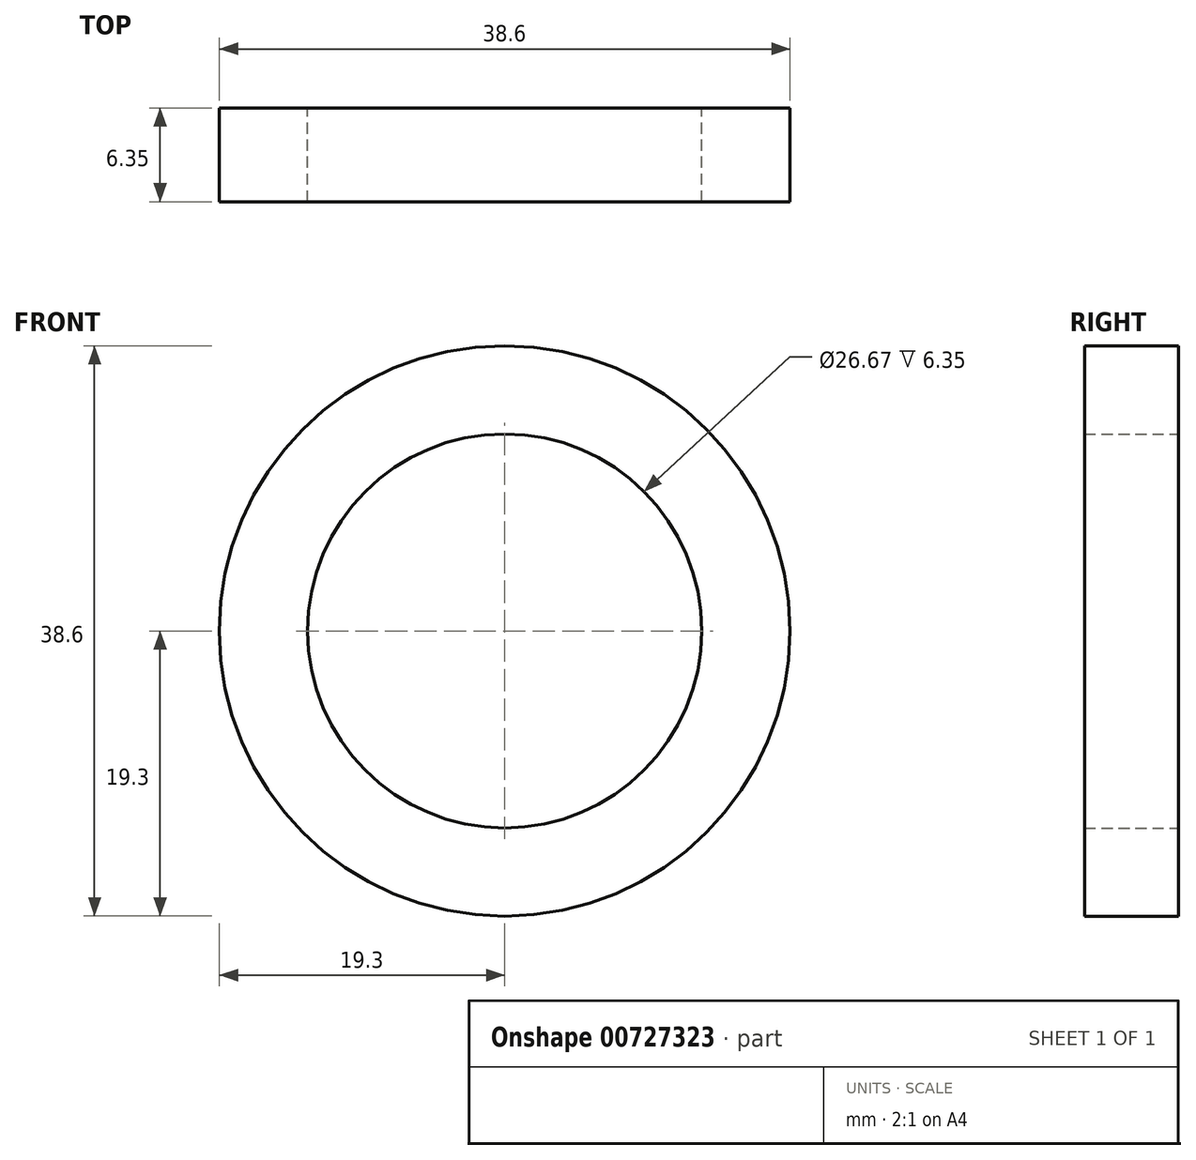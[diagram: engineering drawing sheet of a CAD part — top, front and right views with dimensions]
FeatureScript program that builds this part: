
annotation { "Feature Type Name" : "Feature", "Feature Type Description" : "" }
export const myFeature = defineFeature(function(context is Context, id is Id, definition is map)
    precondition{}
    {
        {
            var Q0;
            Q0=qCreatedBy(makeId("Front.planeOp"),FACE);
            var sketch = newSketch(context, id + "F0", { "sketchPlane" : qUnion([Q0])});
            skCircle(sketch, "E0", {"center": v(0, 0) * mm, "radius": 19.3 * mm});
            skCircle(sketch, "E1", {"center": v(0, 0) * mm, "radius": 13.33 * mm});
            skSolve(sketch);
        }
        {
            var Q0;
            Q0=makeQuery(id+"F0.imprint","IMPRINT",FACE,{"disambiguationData":[TD([[makeQuery(id+"F0.imprint","IMPRINT",EDGE,{"derivedFrom":sQuery(id+"F0.wireOp",EDGE,"E0")}),1.0]])]});
            extrude(context, id + "F1", {"entities" : qUnion([Q0]), "depth" : 6.35 * mm, "offsetDistance" : 25.4 * mm});
        }
    });
